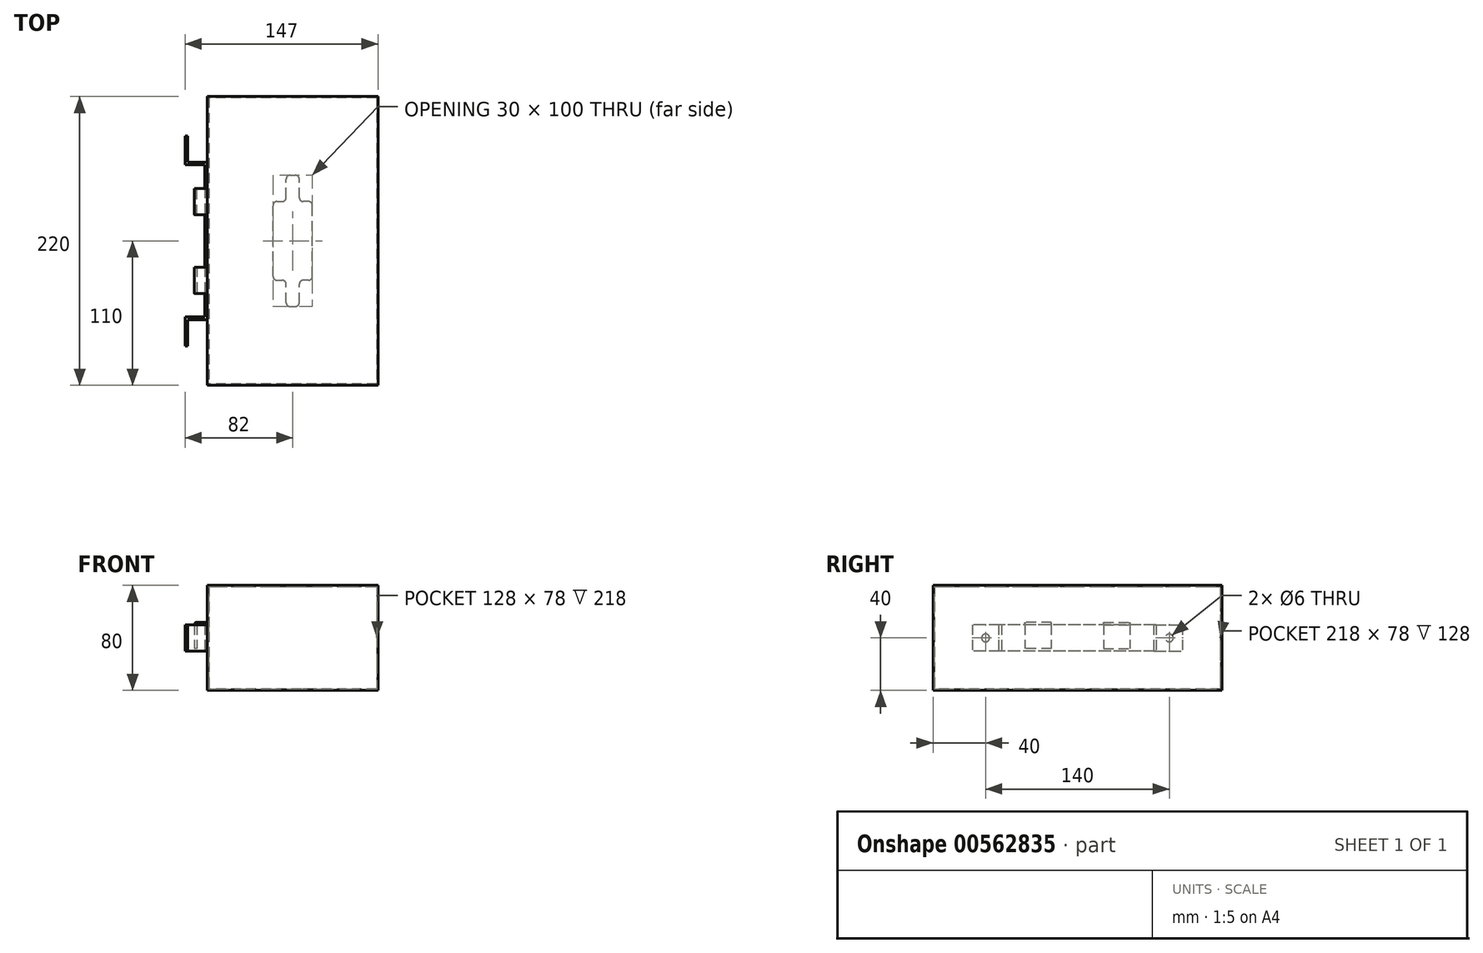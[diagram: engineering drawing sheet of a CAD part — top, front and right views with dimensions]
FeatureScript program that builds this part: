
annotation { "Feature Type Name" : "Feature", "Feature Type Description" : "" }
export const myFeature = defineFeature(function(context is Context, id is Id, definition is map)
    precondition{}
    {
        {
            var Q0;
            Q0=qCreatedBy(makeId("Top.planeOp"),FACE);
            var sketch = newSketch(context, id + "F0", { "sketchPlane" : qUnion([Q0])});
            skLineSegment(sketch, "E0.bottom", {"start": v(65, 110) * mm, "end": v(-65, 110) * mm});
            skLineSegment(sketch, "E0.top", {"start": v(65, -110) * mm, "end": v(-65, -110) * mm});
            skLineSegment(sketch, "E0.left", {"start": v(65, 110) * mm, "end": v(65, -110) * mm});
            skLineSegment(sketch, "E0.right", {"start": v(-65, 110) * mm, "end": v(-65, -110) * mm});
            skPoint(sketch, "E0.middle", {"position": v(0, 0) * mm});
            skSolve(sketch);
        }
        {
            var Q0;
            Q0=qSketchRegion(id+"F0",true);
            extrude(context, id + "F1", {"entities" : qUnion([Q0]), "endBound" : BoundingType.SYMMETRIC, "depth" : 80 * mm, "offsetDistance" : 25 * mm});
        }
        {
            var Q0;
            Q0=makeQuery(id+"F1.opExtrude","SWEPT_FACE",FACE,{"disambiguationData":[OSD([sQuery(id+"F0.wireOp",EDGE,"E0.left")])]});
            var Q1;
            Q1=makeQuery(id+"F1.opExtrude","SWEPT_FACE",FACE,{"disambiguationData":[OSD([sQuery(id+"F0.wireOp",EDGE,"E0.top")])]});
            var Q2;
            Q2=makeQuery(id+"F1.opExtrude","CAP_FACE",FACE,{"disambiguationData":[OSD([sQuery(id+"F0.wireOp",EDGE,"E0.bottom"),sQuery(id+"F0.wireOp",EDGE,"E0.top"),sQuery(id+"F0.wireOp",EDGE,"E0.left"),sQuery(id+"F0.wireOp",EDGE,"E0.right")])],"isStart":false});
            var Q3;
            Q3=makeQuery(id+"F1.opExtrude","SWEPT_FACE",FACE,{"disambiguationData":[OSD([sQuery(id+"F0.wireOp",EDGE,"E0.right")])]});
            var Q4;
            Q4=makeQuery(id+"F1.opExtrude","SWEPT_BODY",BODY,{"disambiguationData":[OSD([sQuery(id+"F0.wireOp",EDGE,"E0.bottom"),sQuery(id+"F0.wireOp",EDGE,"E0.top"),sQuery(id+"F0.wireOp",EDGE,"E0.left"),sQuery(id+"F0.wireOp",EDGE,"E0.right")])]});
            shell(context, id + "F2", {"isHollow" : true, "entities" : qUnion([Q0, Q1, Q2, Q3]), "parts" : qUnion([Q4]), "thickness" : 1 * mm});
        }
        {
            var Q0;
            Q0=makeQuery(id+"F1.opExtrude","CAP_FACE",FACE,{"disambiguationData":[OSD([sQuery(id+"F0.wireOp",EDGE,"E0.bottom"),sQuery(id+"F0.wireOp",EDGE,"E0.top"),sQuery(id+"F0.wireOp",EDGE,"E0.left"),sQuery(id+"F0.wireOp",EDGE,"E0.right")])],"isStart":true});
            var sketch = newSketch(context, id + "F3", { "sketchPlane" : qUnion([Q0])});
            skPoint(sketch, "E1.orphan", {"position": v(58.75, -193.86) * mm});
            skLineSegment(sketch, "E2.bottom", {"start": v(-2, 50) * mm, "end": v(2, 50) * mm});
            skLineSegment(sketch, "E2.top", {"start": v(-2, -50) * mm, "end": v(2, -50) * mm});
            skLineSegment(sketch, "E2.left", {"start": v(-5, 47) * mm, "end": v(-5, 33) * mm});
            skLineSegment(sketch, "E2.right", {"start": v(5, 47) * mm, "end": v(5, 33) * mm});
            skPoint(sketch, "E2.middle", {"position": v(0, 0) * mm});
            skLineSegment(sketch, "E3.bottom", {"start": v(-12, 30) * mm, "end": v(-8, 30) * mm});
            skLineSegment(sketch, "E3.top", {"start": v(-12, -30) * mm, "end": v(-8, -30) * mm});
            skLineSegment(sketch, "E3.left", {"start": v(-15, 27) * mm, "end": v(-15, -27) * mm});
            skPoint(sketch, "E3.middle", {"position": v(-5, 0) * mm});
            skLineSegment(sketch, "E4.bottom", {"start": v(12, 30) * mm, "end": v(8, 30) * mm});
            skLineSegment(sketch, "E4.top", {"start": v(12, -30) * mm, "end": v(8, -30) * mm});
            skLineSegment(sketch, "E4.left", {"start": v(15, 27) * mm, "end": v(15, -27) * mm});
            skPoint(sketch, "E4.middle", {"position": v(5, 0) * mm});
            skPoint(sketch, "E3.right.start.orphan", {"position": v(5, 30) * mm});
            skPoint(sketch, "E5.orphan", {"position": v(5, -30) * mm});
            skLineSegment(sketch, "E6.trimOffspring", {"start": v(-5, -33) * mm, "end": v(-5, -47) * mm});
            skLineSegment(sketch, "E7.trimOffspring", {"start": v(5, -33) * mm, "end": v(5, -47) * mm});
            skPoint(sketch, "E8.visualSharp", {"position": v(-15, 30) * mm});
            skArc(sketch, "E8.filletArc", {"start": v(-12, 30) * mm, "mid": v(-14.12, 29.12) * mm, "end": v(-15, 27) * mm});
            skPoint(sketch, "E9.visualSharp", {"position": v(-5, 30) * mm});
            skArc(sketch, "E9.filletArc", {"start": v(-8, 30) * mm, "mid": v(-5.88, 30.88) * mm, "end": v(-5, 33) * mm});
            skArc(sketch, "E10.filletArc", {"start": v(5, 33) * mm, "mid": v(5.88, 30.88) * mm, "end": v(8, 30) * mm});
            skPoint(sketch, "E11.visualSharp", {"position": v(15, 30) * mm});
            skArc(sketch, "E11.filletArc", {"start": v(15, 27) * mm, "mid": v(14.12, 29.12) * mm, "end": v(12, 30) * mm});
            skPoint(sketch, "E12.visualSharp", {"position": v(15, -30) * mm});
            skArc(sketch, "E12.filletArc", {"start": v(12, -30) * mm, "mid": v(14.12, -29.12) * mm, "end": v(15, -27) * mm});
            skArc(sketch, "E13.filletArc", {"start": v(8, -30) * mm, "mid": v(5.88, -30.88) * mm, "end": v(5, -33) * mm});
            skPoint(sketch, "E14.visualSharp", {"position": v(-5, -30) * mm});
            skArc(sketch, "E14.filletArc", {"start": v(-5, -33) * mm, "mid": v(-5.88, -30.88) * mm, "end": v(-8, -30) * mm});
            skPoint(sketch, "E15.visualSharp", {"position": v(-15, -30) * mm});
            skArc(sketch, "E15.filletArc", {"start": v(-15, -27) * mm, "mid": v(-14.12, -29.12) * mm, "end": v(-12, -30) * mm});
            skPoint(sketch, "E16.visualSharp", {"position": v(5, 50) * mm});
            skArc(sketch, "E16.filletArc", {"start": v(5, 47) * mm, "mid": v(4.12, 49.12) * mm, "end": v(2, 50) * mm});
            skPoint(sketch, "E17.visualSharp", {"position": v(-5, 50) * mm});
            skArc(sketch, "E17.filletArc", {"start": v(-2, 50) * mm, "mid": v(-4.12, 49.12) * mm, "end": v(-5, 47) * mm});
            skPoint(sketch, "E18.visualSharp", {"position": v(5, -50) * mm});
            skArc(sketch, "E18.filletArc", {"start": v(2, -50) * mm, "mid": v(4.12, -49.12) * mm, "end": v(5, -47) * mm});
            skPoint(sketch, "E19.visualSharp", {"position": v(-5, -50) * mm});
            skArc(sketch, "E19.filletArc", {"start": v(-5, -47) * mm, "mid": v(-4.12, -49.12) * mm, "end": v(-2, -50) * mm});
            skSolve(sketch);
        }
        {
            var Q0;
            Q0=qSketchRegion(id+"F3",true);
            extrude(context, id + "F4", {"entities" : qUnion([Q0]), "operationType" : NewBodyOperationType.REMOVE, "endBound" : BoundingType.UP_TO_NEXT, "oppositeDirection" : true, "depth" : 440 * mm, "offsetDistance" : 25 * mm});
        }
        {
            var Q0;
            Q0=qCreatedBy(makeId("Top.planeOp"),FACE);
            var sketch = newSketch(context, id + "F5", { "sketchPlane" : qUnion([Q0])});
            skLineSegment(sketch, "E20", {"start": v(-65, 60) * mm, "end": v(-65, -60) * mm});
            skLineSegment(sketch, "E21", {"start": v(-65, 60) * mm, "end": v(-80, 60) * mm});
            skLineSegment(sketch, "E22", {"start": v(-80, 60) * mm, "end": v(-80, 80) * mm});
            skLineSegment(sketch, "E23", {"start": v(-65, -60) * mm, "end": v(-80, -60) * mm});
            skLineSegment(sketch, "E24", {"start": v(-80, -60) * mm, "end": v(-80, -80) * mm});
            skLineSegment(sketch, "E25.0", {"start": v(-82, 58) * mm, "end": v(-82, 80) * mm});
            skLineSegment(sketch, "E25.1", {"start": v(-82, -58) * mm, "end": v(-82, -80) * mm});
            skLineSegment(sketch, "E25.2", {"start": v(-67, -58) * mm, "end": v(-82, -58) * mm});
            skLineSegment(sketch, "E25.3", {"start": v(-67, 58) * mm, "end": v(-67, -58) * mm});
            skLineSegment(sketch, "E25.4", {"start": v(-67, 58) * mm, "end": v(-82, 58) * mm});
            skLineSegment(sketch, "E26", {"start": v(-80, -80) * mm, "end": v(-82, -80) * mm});
            skLineSegment(sketch, "E27", {"start": v(-82, 80) * mm, "end": v(-80, 80) * mm});
            skSolve(sketch);
        }
        {
            var Q0;
            Q0=qSketchRegion(id+"F5",true);
            extrude(context, id + "F6", {"entities" : qUnion([Q0]), "endBound" : BoundingType.SYMMETRIC, "depth" : 20 * mm, "offsetDistance" : 25 * mm});
        }
        {
            var Q0;
            Q0=makeQuery(id+"F6.opExtrude","SWEPT_FACE",FACE,{"disambiguationData":[OSD([sQuery(id+"F5.wireOp",EDGE,"E25.0")])]});
            var sketch = newSketch(context, id + "F7", { "sketchPlane" : qUnion([Q0])});
            skCircle(sketch, "E28", {"center": v(-70, 0) * mm, "radius": 3 * mm});
            skCircle(sketch, "E29", {"center": v(70, 0) * mm, "radius": 3 * mm});
            skSolve(sketch);
        }
        {
            var Q0;
            Q0 = qSketchRegion(id + "F7", true);
            extrude(context, id + "F8", {"entities" : qUnion([Q0]), "operationType" : NewBodyOperationType.REMOVE, "endBound" : BoundingType.UP_TO_NEXT, "oppositeDirection" : true, "depth" : 25 * mm, "offsetDistance" : 25 * mm});
        }
        {
            var Q0;
            Q0=qCreatedBy(makeId("Front.planeOp"),FACE);
            cPlane(context, id + "F9", {"entities" : qUnion([Q0]), "cplaneType" : CPlaneType.OFFSET, "offset" : 30 * mm, "oppositeDirection" : true, "width" : 150 * mm, "height" : 150 * mm});
        }
        {
            var Q0;
            Q0=qCreatedBy(id+"F9.planeOp",FACE);
            var sketch = newSketch(context, id + "F10", { "sketchPlane" : qUnion([Q0])});
            skLineSegment(sketch, "E30", {"start": v(-65, 10) * mm, "end": v(-73, 10) * mm});
            skLineSegment(sketch, "E31", {"start": v(-73, 10) * mm, "end": v(-73, -8) * mm});
            skLineSegment(sketch, "E32.0", {"start": v(-75, 10) * mm, "end": v(-75, -8) * mm});
            skLineSegment(sketch, "E32.1", {"start": v(-65, 12) * mm, "end": v(-73, 12) * mm});
            skLineSegment(sketch, "E33", {"start": v(-65, 10) * mm, "end": v(-65, 12) * mm});
            skLineSegment(sketch, "E34", {"start": v(-73, -8) * mm, "end": v(-75, -8) * mm});
            skPoint(sketch, "E35.visualSharp", {"position": v(-75, 12) * mm});
            skArc(sketch, "E35.filletArc", {"start": v(-73, 12) * mm, "mid": v(-74.41, 11.41) * mm, "end": v(-75, 10) * mm});
            skSolve(sketch);
        }
        {
            var Q0;
            Q0 = qSketchRegion(id + "F10", true);
            extrude(context, id + "F11", {"entities" : qUnion([Q0]), "endBound" : BoundingType.SYMMETRIC, "depth" : 20 * mm, "offsetDistance" : 25 * mm});
        }
        {
            var Q0;
            Q0=makeQuery(id+"F11.opExtrude","SWEPT_BODY",BODY,{"disambiguationData":[OSD([sQuery(id+"F10.wireOp",EDGE,"E30"),sQuery(id+"F10.wireOp",EDGE,"E31"),sQuery(id+"F10.wireOp",EDGE,"E32.0"),sQuery(id+"F10.wireOp",EDGE,"E32.1"),sQuery(id+"F10.wireOp",EDGE,"E33"),sQuery(id+"F10.wireOp",EDGE,"E34"),sQuery(id+"F10.wireOp",EDGE,"E35.filletArc")])]});
            var Q1;
            Q1=qCreatedBy(makeId("Front.planeOp"),FACE);
            mirror(context, id + "F12", {"entities" : qUnion([Q0]), "mirrorPlane" : qUnion([Q1])});
        }
    });
